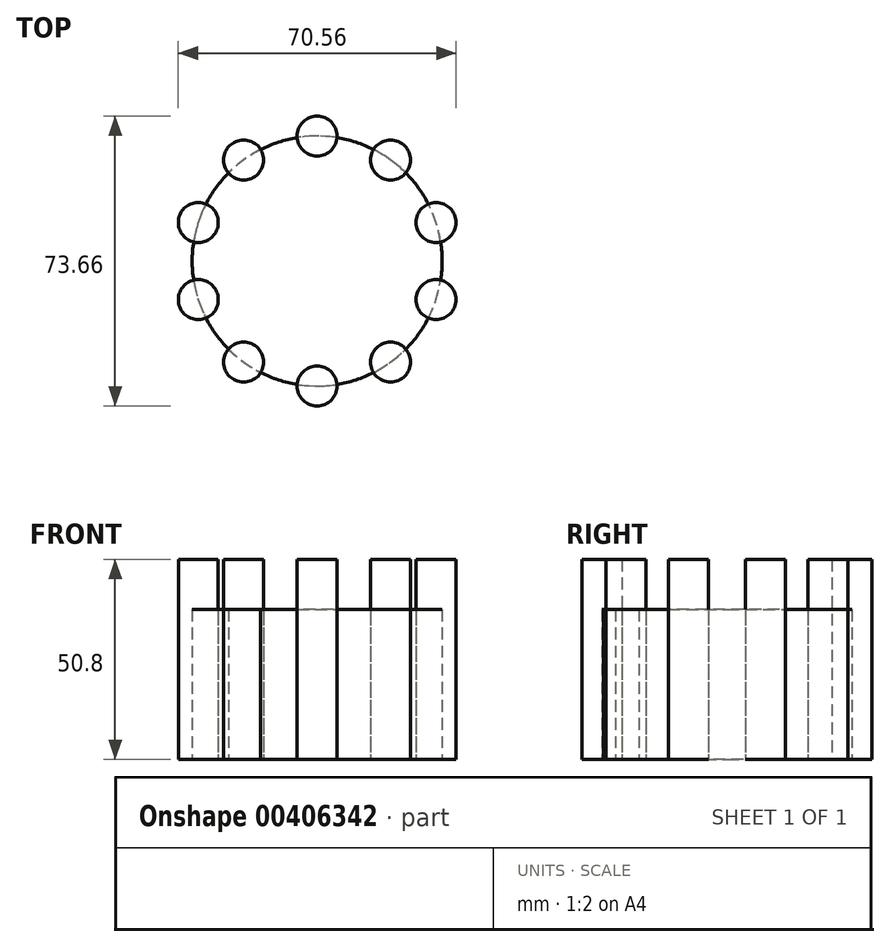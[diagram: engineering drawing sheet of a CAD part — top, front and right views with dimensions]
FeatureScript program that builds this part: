
annotation { "Feature Type Name" : "Feature", "Feature Type Description" : "" }
export const myFeature = defineFeature(function(context is Context, id is Id, definition is map)
    precondition{}
    {
        {
            var Q0;
            Q0=qCreatedBy(makeId("Top.planeOp"),FACE);
            var sketch = newSketch(context, id + "F0", { "sketchPlane" : qUnion([Q0])});
            skCircle(sketch, "E0", {"center": v(0, 0) * mm, "radius": 31.75 * mm});
            skSolve(sketch);
        }
        {
            var Q0;
            Q0=qSketchRegion(id+"F0",true);
            extrude(context, id + "F1", {"entities" : qUnion([Q0]), "depth" : 38.1 * mm});
        }
        {
            var Q0;
            Q0=qCreatedBy(makeId("Top.planeOp"),FACE);
            var sketch = newSketch(context, id + "F2", { "sketchPlane" : qUnion([Q0])});
            skCircle(sketch, "E1", {"center": v(0, 31.75) * mm, "radius": 5.08 * mm});
            skCircle(sketch, "E2.1.0", {"center": v(-18.66, 25.69) * mm, "radius": 5.08 * mm});
            skCircle(sketch, "E2.2.0", {"center": v(-30.2, 9.81) * mm, "radius": 5.08 * mm});
            skCircle(sketch, "E2.3.0", {"center": v(-30.2, -9.81) * mm, "radius": 5.08 * mm});
            skCircle(sketch, "E2.4.0", {"center": v(-18.66, -25.69) * mm, "radius": 5.08 * mm});
            skCircle(sketch, "E2.5.0", {"center": v(0, -31.75) * mm, "radius": 5.08 * mm});
            skCircle(sketch, "E2.6.0", {"center": v(18.66, -25.69) * mm, "radius": 5.08 * mm});
            skCircle(sketch, "E2.7.0", {"center": v(30.2, -9.81) * mm, "radius": 5.08 * mm});
            skCircle(sketch, "E2.8.0", {"center": v(30.2, 9.81) * mm, "radius": 5.08 * mm});
            skCircle(sketch, "E2.9.0", {"center": v(18.66, 25.69) * mm, "radius": 5.08 * mm});
            skPoint(sketch, "E2.center", {"position": v(0, 0) * mm});
            skSolve(sketch);
        }
        {
            var Q0;
            Q0=qSketchRegion(id+"F2",true);
            extrude(context, id + "F3", {"entities" : qUnion([Q0]), "depth" : 50.8 * mm});
        }
        {
            var Q0;
            Q0=makeQuery(id+"F3.opExtrude","SWEPT_BODY",BODY,{"disambiguationData":[OSD([sQuery(id+"F2.wireOp",EDGE,"E2.5.0")])]});
            var Q1;
            Q1=makeQuery(id+"F1.opExtrude","SWEPT_BODY",BODY,{"disambiguationData":[OSD([sQuery(id+"F0.wireOp",EDGE,"E0")])]});
            booleanBodies(context, id + "F4", {"operationType" : BooleanOperationType.INTERSECTION, "tools" : qUnion([Q0, Q1]), "keepTools" : true});
        }
        {
            var Q0;
            Q0=makeQuery(id+"F1.opExtrude","SWEPT_BODY",BODY,{"disambiguationData":[OSD([sQuery(id+"F0.wireOp",EDGE,"E0")])]});
            var Q1;
            Q1=makeQuery(id+"F3.opExtrude","SWEPT_BODY",BODY,{"disambiguationData":[OSD([sQuery(id+"F2.wireOp",EDGE,"E2.4.0")])]});
            booleanBodies(context, id + "F5", {"operationType" : BooleanOperationType.INTERSECTION, "tools" : qUnion([Q0, Q1]), "keepTools" : true});
        }
    });
